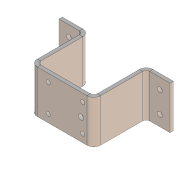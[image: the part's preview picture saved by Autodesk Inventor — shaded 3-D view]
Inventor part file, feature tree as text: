
AUTODESK INVENTOR PART (.ipt)
format: ipt  version: 2016 (Build 200138000, 138)  size: 165,888 bytes
history: native  units: in
note: dims shown in document units (in); Inventor stores cm internally (conversion verified against a paired STEP export)
features: sheet_metal_op x7, sketch x4, other x3, projected_geometry x2, hole x1
ambient origin geometry x8: Origin, YZ Plane, XZ Plane, XY Plane, X Axis, Y Axis, Z Axis, Center Point
bodies: Solid1 (feature_tree)
feature tree (17):
  sheet_metal_op  "Face1"
  sheet_metal_op  "Flange3"
  sheet_metal_op  "Flange4"
  hole  "Hole1"  [1 undecoded]
  sketch  "Sketch1"  dims[d2=1.5748in d3=1.8238in]
  other  "Plate1"
  sketch  "Sketch4"  dims[d4=0.125in]
  other  "Plate4"
  sheet_metal_op  "Bend3"
  sheet_metal_op  "Corner3"
  sketch  "Sketch5"  dims[d25=0.125in]
  other  "Plate5"
  sheet_metal_op  "Bend4"
  sheet_metal_op  "Corner4"
  sketch  "Sketch6"  dims[d26=0.0625in d27=0.25in d28=0.125in d29=2.045in d30=90.0deg d31=0.125in d32=0.5in d33=0.125in d34=0.125in d35=0.125in d36=0.0625in d37=0.25in d38=0.125in d39=1.0in d40=90.0deg d41=0.125in d42=0.5in d43=0.125in d44=0.125in d45=0.19in d46=0.75in d47=0.375in d48=0.25in d49=0.5635in d50=0.125in d51=0.8108in]
  projected_geometry  "Projected Loop1"
  projected_geometry  "Projected Loop2"
note: 1 required parameter value undecoded (feature->parameter linkage not recoverable at this tier; creation-order binding heuristic only, values carry confidence <= 0.55)
